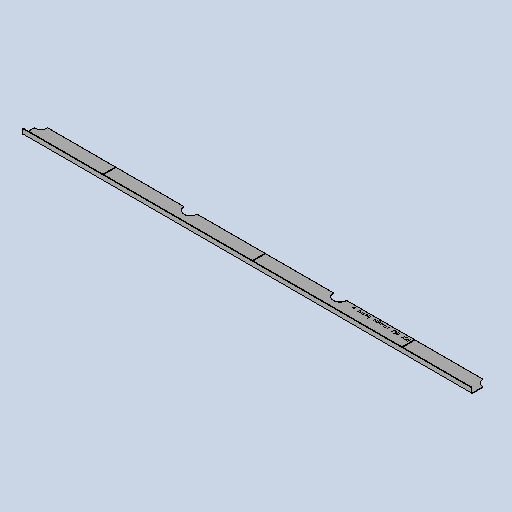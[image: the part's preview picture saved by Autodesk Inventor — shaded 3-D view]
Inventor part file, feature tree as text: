
AUTODESK INVENTOR PART (.ipt)
format: ipt  version: 2025 (Build 290162010, 162A)  size: 336,896 bytes
history: native  units: mm
features: sketch x6, other x5, sheet_metal_op x4, extrude x3, mirror x2, pattern_linear x1, projected_geometry x1
ambient origin geometry x8: Origin, YZ Plane, XZ Plane, XY Plane, X Axis, Y Axis, Z Axis, Center Point
bodies: Solid1 (feature_tree)
feature tree (22):
  sheet_metal_op  "Face1"
  sheet_metal_op  "Flange1"
  extrude  "Extrusion1"  Depth=62.0mm
  pattern_linear  "Rectangular Pattern1"  Count1=2 Spacing1=90.0deg
  extrude  "Extrusion2"  Depth=8.0mm
  mirror  "Mirror1"
  extrude  "Extrusion3"  Depth=2.0mm
  mirror  "Mirror2"
  other  "Mark2"
  other  "A-Side Definition"
  sketch  "Sketch1"  dims[d0=1500.0mm d1=62.0mm]
  other  "Plate1"
  sketch  "Sketch2"  dims[d2=2.0mm]
  other  "Plate2"
  sheet_metal_op  "Bend1"
  sheet_metal_op  "Corner1"
  sketch  "Sketch5"  dims[d3=2.0mm]
  sketch  "Sketch6"  dims[d4=1.0mm]
  sketch  "Sketch7"  dims[d5=4.0mm]
  projected_geometry  "Projected Loop3"
  sketch  "Sketch8"  dims[d6=2.75mm d7=20.0mm d8=90.0deg d9=2.75mm d10=8.0mm d11=2.0mm d12=2.75mm d15=0.0mm d16=0.0mm d18=2.0mm d21=30.0mm d23=500.0mm d24=45.0mm d25=30.0mm d26=0.0mm d27=2.0mm d28=20.0mm d29=100.0mm d30=10.0mm d31=0.0mm d32=0.0mm d33=200.0mm d34=12.0mm d37=5.0mm d38=5.0mm]
  other  "Definition1"
